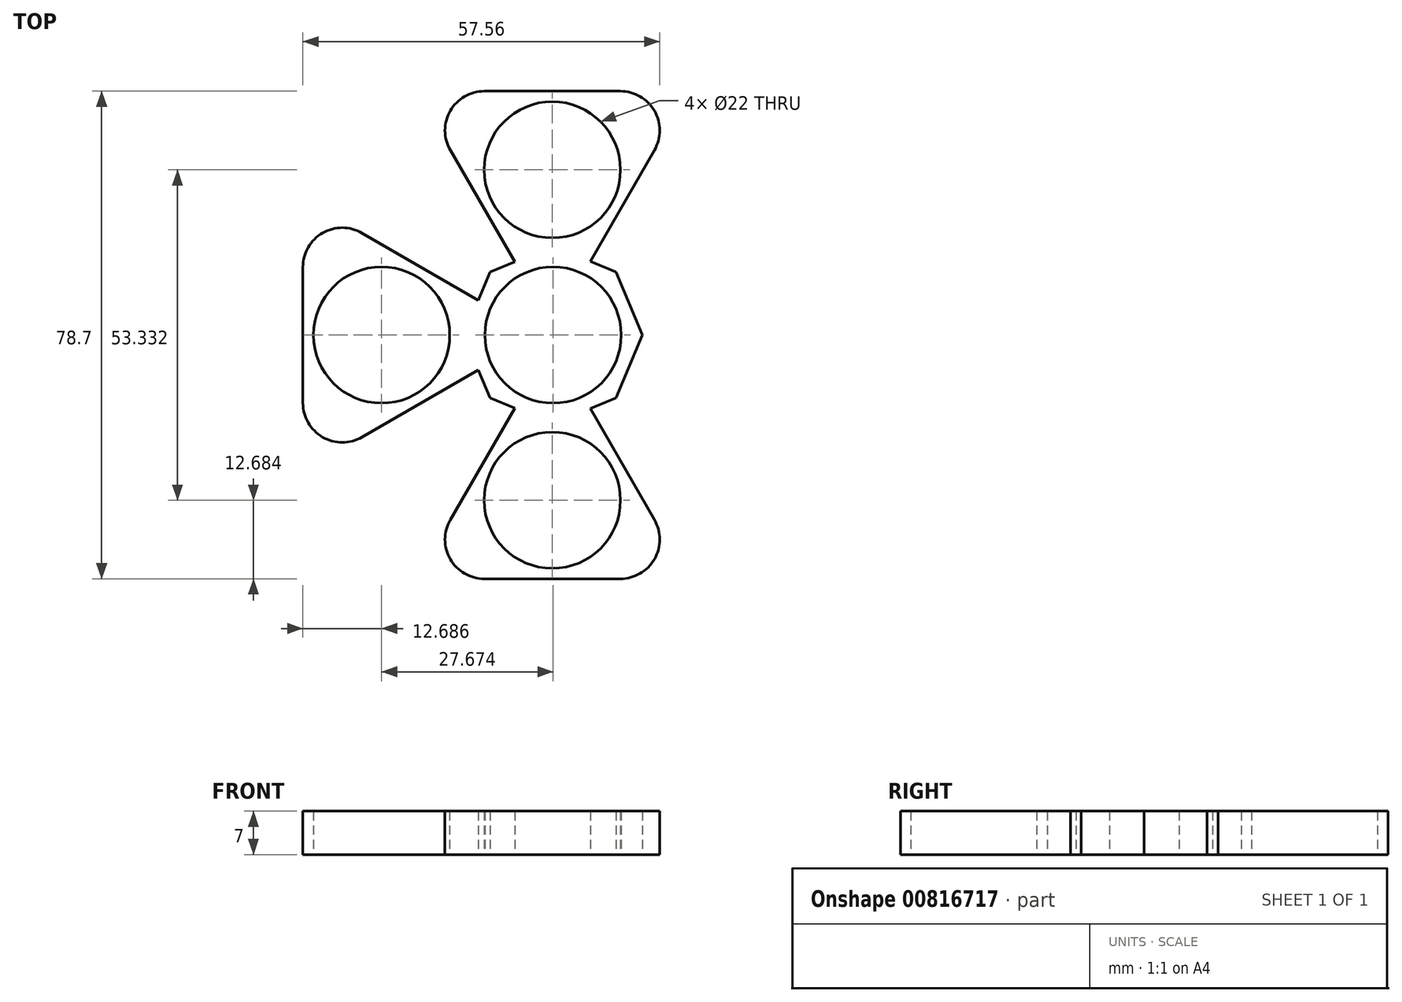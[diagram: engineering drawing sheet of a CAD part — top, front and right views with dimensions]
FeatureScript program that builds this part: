
annotation { "Feature Type Name" : "Feature", "Feature Type Description" : "" }
export const myFeature = defineFeature(function(context is Context, id is Id, definition is map)
    precondition{}
    {
        {
            var Q0;
            Q0=qCreatedBy(makeId("Top.planeOp"),FACE);
            var sketch = newSketch(context, id + "F0", { "sketchPlane" : qUnion([Q0])});
            skCircle(sketch, "E0.cCircle", {"center": v(0, 0) * mm, "radius": 13.28 * mm, "construction": true});
            skLineSegment(sketch, "E0.0", {"start": v(0, 14.38) * mm, "end": v(10.17, 10.17) * mm});
            skLineSegment(sketch, "E0.1", {"start": v(10.17, 10.17) * mm, "end": v(14.38, 0) * mm});
            skLineSegment(sketch, "E0.2", {"start": v(14.38, 0) * mm, "end": v(10.17, -10.17) * mm});
            skLineSegment(sketch, "E0.3", {"start": v(10.17, -10.17) * mm, "end": v(0, -14.38) * mm});
            skLineSegment(sketch, "E0.4", {"start": v(0, -14.38) * mm, "end": v(-10.17, -10.17) * mm});
            skLineSegment(sketch, "E0.5", {"start": v(-10.17, -10.17) * mm, "end": v(-14.38, 0) * mm});
            skLineSegment(sketch, "E0.6", {"start": v(-14.38, 0) * mm, "end": v(-10.17, 10.17) * mm});
            skLineSegment(sketch, "E0.7", {"start": v(-10.17, 10.17) * mm, "end": v(0, 14.38) * mm});
            skCircle(sketch, "E1", {"center": v(0, 0) * mm, "radius": 11 * mm});
            skCircle(sketch, "E2.cCircle", {"center": v(-27.67, 0) * mm, "radius": 11 * mm, "construction": true});
            skLineSegment(sketch, "E2.0", {"start": v(-38.67, -8.05) * mm, "end": v(-38.67, 8.05) * mm});
            skLineSegment(sketch, "E2.1", {"start": v(-29.15, 13.55) * mm, "end": v(-12.66, 4.03) * mm});
            skLineSegment(sketch, "E2.2", {"start": v(-12.66, -4.03) * mm, "end": v(-29.15, -13.55) * mm});
            skPoint(sketch, "E2.0.midPoint", {"position": v(-38.67, 0) * mm});
            skCircle(sketch, "E3.cCircle", {"center": v(-27.67, 0) * mm, "radius": 12.69 * mm, "construction": true});
            skLineSegment(sketch, "E3.0", {"start": v(-40.36, -10.98) * mm, "end": v(-40.36, 10.98) * mm});
            skLineSegment(sketch, "E3.1", {"start": v(-30.84, 16.47) * mm, "end": v(-12.04, 5.62) * mm});
            skLineSegment(sketch, "E3.2", {"start": v(-12.04, -5.62) * mm, "end": v(-30.84, -16.47) * mm});
            skPoint(sketch, "E3.0.midPoint", {"position": v(-40.36, 0) * mm});
            skCircle(sketch, "E4.cCircle", {"center": v(-0.12, -26.67) * mm, "radius": 11 * mm, "construction": true});
            skLineSegment(sketch, "E4.0", {"start": v(-13.68, -28.14) * mm, "end": v(-4.62, -12.45) * mm});
            skLineSegment(sketch, "E4.2", {"start": v(7.93, -37.67) * mm, "end": v(-8.18, -37.67) * mm});
            skPoint(sketch, "E4.0.midPoint", {"position": v(-9.65, -21.17) * mm});
            skCircle(sketch, "E5.cCircle", {"center": v(-0.12, -26.67) * mm, "radius": 12.69 * mm, "construction": true});
            skLineSegment(sketch, "E5.0", {"start": v(-16.6, -29.83) * mm, "end": v(-6.17, -11.76) * mm});
            skLineSegment(sketch, "E5.1", {"start": v(5.98, -11.86) * mm, "end": v(16.35, -29.83) * mm});
            skLineSegment(sketch, "E5.2", {"start": v(10.85, -39.35) * mm, "end": v(-11.1, -39.35) * mm});
            skPoint(sketch, "E5.0.midPoint", {"position": v(-11.1, -20.32) * mm});
            skPoint(sketch, "E6.orphan", {"position": v(-5.67, 0) * mm});
            skPoint(sketch, "E7.orphan", {"position": v(-2.3, 0) * mm});
            skPoint(sketch, "E8.orphan", {"position": v(0, 5.12) * mm});
            skPoint(sketch, "E9.orphan", {"position": v(0, 1.74) * mm});
            skPoint(sketch, "E10.orphan", {"position": v(5.18, 0.1) * mm});
            skPoint(sketch, "E11.orphan", {"position": v(1.8, 0.1) * mm});
            skPoint(sketch, "E12.orphan", {"position": v(-0.12, -1.3) * mm});
            skLineSegment(sketch, "E13.trimOffspring", {"start": v(4.42, -12.53) * mm, "end": v(13.43, -28.14) * mm});
            skPoint(sketch, "E4.1.start.orphan", {"position": v(-0.12, -4.67) * mm});
            skPoint(sketch, "E14.visualSharp", {"position": v(-22.1, -39.35) * mm});
            skArc(sketch, "E14.filletArc", {"start": v(-16.6, -29.83) * mm, "mid": v(-16.6, -36.18) * mm, "end": v(-11.1, -39.35) * mm});
            skPoint(sketch, "E15.visualSharp", {"position": v(-19.17, -37.67) * mm});
            skArc(sketch, "E15.filletArc", {"start": v(-13.68, -28.14) * mm, "mid": v(-13.68, -34.5) * mm, "end": v(-8.18, -37.67) * mm});
            skPoint(sketch, "E16.visualSharp", {"position": v(18.93, -37.67) * mm});
            skArc(sketch, "E16.filletArc", {"start": v(7.93, -37.67) * mm, "mid": v(13.43, -34.5) * mm, "end": v(13.43, -28.14) * mm});
            skPoint(sketch, "E17.visualSharp", {"position": v(21.85, -39.35) * mm});
            skArc(sketch, "E17.filletArc", {"start": v(10.85, -39.35) * mm, "mid": v(16.35, -36.18) * mm, "end": v(16.35, -29.83) * mm});
            skPoint(sketch, "E18.visualSharp", {"position": v(-40.36, -21.97) * mm});
            skArc(sketch, "E18.filletArc", {"start": v(-40.36, -10.98) * mm, "mid": v(-37.19, -16.47) * mm, "end": v(-30.84, -16.47) * mm});
            skPoint(sketch, "E19.visualSharp", {"position": v(-38.67, -19.05) * mm});
            skArc(sketch, "E19.filletArc", {"start": v(-38.67, -8.05) * mm, "mid": v(-35.5, -13.55) * mm, "end": v(-29.15, -13.55) * mm});
            skPoint(sketch, "E20.visualSharp", {"position": v(-38.67, 19.05) * mm});
            skArc(sketch, "E20.filletArc", {"start": v(-29.15, 13.55) * mm, "mid": v(-35.5, 13.55) * mm, "end": v(-38.67, 8.05) * mm});
            skPoint(sketch, "E21.visualSharp", {"position": v(-40.36, 21.97) * mm});
            skArc(sketch, "E21.filletArc", {"start": v(-30.84, 16.47) * mm, "mid": v(-37.19, 16.47) * mm, "end": v(-40.36, 10.98) * mm});
            skLineSegment(sketch, "E22.MirrorCS", {"start": v(29.15, 13.55) * mm, "end": v(12.66, 4.03) * mm});
            skLineSegment(sketch, "E23.MirrorCS", {"start": v(30.84, 16.47) * mm, "end": v(12.04, 5.62) * mm});
            skArc(sketch, "E24.MirrorCS", {"start": v(30.84, 16.47) * mm, "mid": v(37.19, 16.47) * mm, "end": v(40.36, 10.98) * mm});
            skLineSegment(sketch, "E25.MirrorCS", {"start": v(40.36, -10.98) * mm, "end": v(40.36, 10.98) * mm});
            skArc(sketch, "E26.MirrorCS", {"start": v(40.36, -10.98) * mm, "mid": v(37.19, -16.47) * mm, "end": v(30.84, -16.47) * mm});
            skLineSegment(sketch, "E27.MirrorCS", {"start": v(12.04, -5.62) * mm, "end": v(30.84, -16.47) * mm});
            skLineSegment(sketch, "E28.MirrorCS", {"start": v(38.67, -8.05) * mm, "end": v(38.67, 8.05) * mm});
            skLineSegment(sketch, "E29.MirrorCS", {"start": v(12.66, -4.03) * mm, "end": v(29.15, -13.55) * mm});
            skArc(sketch, "E30.MirrorCS", {"start": v(38.67, -8.05) * mm, "mid": v(35.5, -13.55) * mm, "end": v(29.15, -13.55) * mm});
            skCircle(sketch, "E31.MirrorC", {"center": v(27.67, 0) * mm, "radius": 11 * mm, "construction": true});
            skCircle(sketch, "E32.MirrorC", {"center": v(-0.12, 26.67) * mm, "radius": 11 * mm, "construction": true});
            skLineSegment(sketch, "E33.MirrorCS", {"start": v(5.98, 11.86) * mm, "end": v(16.35, 29.83) * mm});
            skLineSegment(sketch, "E34.MirrorCS", {"start": v(-16.6, 29.83) * mm, "end": v(-6.17, 11.76) * mm});
            skLineSegment(sketch, "E35.MirrorCS", {"start": v(10.85, 39.35) * mm, "end": v(-11.1, 39.35) * mm});
            skArc(sketch, "E36.MirrorCS", {"start": v(-16.6, 29.83) * mm, "mid": v(-16.6, 36.18) * mm, "end": v(-11.1, 39.35) * mm});
            skArc(sketch, "E37.MirrorCS", {"start": v(10.85, 39.35) * mm, "mid": v(16.35, 36.18) * mm, "end": v(16.35, 29.83) * mm});
            skSolve(sketch);
        }
        {
            var Q0;
            Q0=makeQuery(id+"F0.imprint","IMPRINT",FACE,{"disambiguationData":[TD([[makeQuery(id+"F0.imprint","IMPRINT",EDGE,{"derivedFrom":sQuery(id+"F0.wireOp",EDGE,"E4.2")}),1.0]])]});
            var Q1;
            {var subQ10=sQuery(id+"F0.wireOp",EDGE,"E24.MirrorCS");Q1=makeQuery(id+"F0.imprint","IMPRINT",FACE,{"disambiguationData":[TD([[makeQuery(id+"F0.imprint","IMPRINT",EDGE,{"derivedFrom":subQ10}),-1.0]])]});}
            var Q2;
            Q2=makeQuery(id+"F0.imprint","IMPRINT",FACE,{"disambiguationData":[TD([[makeQuery(id+"F0.imprint","IMPRINT",EDGE,{"derivedFrom":sQuery(id+"F0.wireOp",EDGE,"E2.0")}),1.0]])]});
            var Q3;
            Q3=makeQuery(id+"F0.imprint","IMPRINT",FACE,{"disambiguationData":[TD([[makeQuery(id+"F0.imprint","IMPRINT",EDGE,{"derivedFrom":sQuery(id+"F0.wireOp",EDGE,"E4.2")}),-1.0]])]});
            var Q4;
            Q4=makeQuery(id+"F0.imprint","IMPRINT",FACE,{"disambiguationData":[TD([[makeQuery(id+"F0.imprint","IMPRINT",EDGE,{"derivedFrom":sQuery(id+"F0.wireOp",EDGE,"E1")}),-1.0]])]});
            var Q5;
            Q5=makeQuery(id+"F0.imprint","IMPRINT",FACE,{"disambiguationData":[TD([[makeQuery(id+"F0.imprint","IMPRINT",EDGE,{"derivedFrom":sQuery(id+"F0.wireOp",EDGE,"E35.MirrorCS")}),1.0]])]});
            var Q6;
            Q6=makeQuery(id+"F0.imprint","IMPRINT",FACE,{"disambiguationData":[TD([[makeQuery(id+"F0.imprint","IMPRINT",EDGE,{"derivedFrom":sQuery(id+"F0.wireOp",EDGE,"E2.0")}),-1.0]])]});
            var Q7;
            Q7=makeQuery(id+"F0.imprint","IMPRINT",FACE,{"disambiguationData":[TD([[makeQuery(id+"F0.imprint","IMPRINT",EDGE,{"derivedFrom":sQuery(id+"F0.wireOp",EDGE,"E1")}),1.0]])]});
            extrude(context, id + "F1", {"entities" : qUnion([Q0, Q1, Q2, Q3, Q4, Q5, Q6, Q7]), "depth" : 7 * mm, "offsetDistance" : 25.4 * mm});
        }
        {
            var Q0;
            Q0=sQuery(id+"F0.wireOp",VERTEX,"E2.cCircle.center");
            var Q1;
            Q1=sQuery(id+"F0.wireOp",VERTEX,"E4.cCircle.center");
            var Q2;
            Q2=sQuery(id+"F0.wireOp",VERTEX,"E0.cCircle.center");
            var Q3;
            Q3=sQuery(id+"F0.wireOp",VERTEX,"E31.MirrorC.center");
            var Q4;
            Q4=sQuery(id+"F0.wireOp",VERTEX,"E32.MirrorC.center");
            var Q5;
            Q5=makeQuery(id+"F1.opExtrude","SWEPT_BODY",BODY,{"disambiguationData":[OSD([sQuery(id+"F0.wireOp",EDGE,"E0.0"),sQuery(id+"F0.wireOp",EDGE,"E0.1"),sQuery(id+"F0.wireOp",EDGE,"E0.2"),sQuery(id+"F0.wireOp",EDGE,"E0.3"),sQuery(id+"F0.wireOp",EDGE,"E0.4"),sQuery(id+"F0.wireOp",EDGE,"E0.5"),sQuery(id+"F0.wireOp",EDGE,"E0.6"),sQuery(id+"F0.wireOp",EDGE,"E0.7"),sQuery(id+"F0.wireOp",EDGE,"E3.0"),sQuery(id+"F0.wireOp",EDGE,"E3.1"),sQuery(id+"F0.wireOp",EDGE,"E3.2"),sQuery(id+"F0.wireOp",EDGE,"E5.0"),sQuery(id+"F0.wireOp",EDGE,"E5.1"),sQuery(id+"F0.wireOp",EDGE,"E5.2"),sQuery(id+"F0.wireOp",EDGE,"E14.filletArc"),sQuery(id+"F0.wireOp",EDGE,"E17.filletArc"),sQuery(id+"F0.wireOp",EDGE,"E18.filletArc"),sQuery(id+"F0.wireOp",EDGE,"E21.filletArc"),sQuery(id+"F0.wireOp",EDGE,"E23.MirrorCS"),sQuery(id+"F0.wireOp",EDGE,"E24.MirrorCS"),sQuery(id+"F0.wireOp",EDGE,"E25.MirrorCS"),sQuery(id+"F0.wireOp",EDGE,"E26.MirrorCS"),sQuery(id+"F0.wireOp",EDGE,"E27.MirrorCS"),sQuery(id+"F0.wireOp",EDGE,"E33.MirrorCS"),sQuery(id+"F0.wireOp",EDGE,"E34.MirrorCS"),sQuery(id+"F0.wireOp",EDGE,"E35.MirrorCS"),sQuery(id+"F0.wireOp",EDGE,"E36.MirrorCS"),sQuery(id+"F0.wireOp",EDGE,"E37.MirrorCS")])]});
            hole(context, id + "F2", {"style" : HoleStyle.SIMPLE, "endStyle" : HoleEndStyle.THROUGH, "oppositeDirection" : true, "holeDiameter" : 22 * mm, "majorDiameter" : 6.35 * mm, "isTappedThrough" : true, "tappedDepth" : 12.7 * mm, "tapClearance" : 3, "locations" : qUnion([Q0, Q1, Q2, Q3, Q4]), "scope" : qUnion([Q5])});
        }
    });
